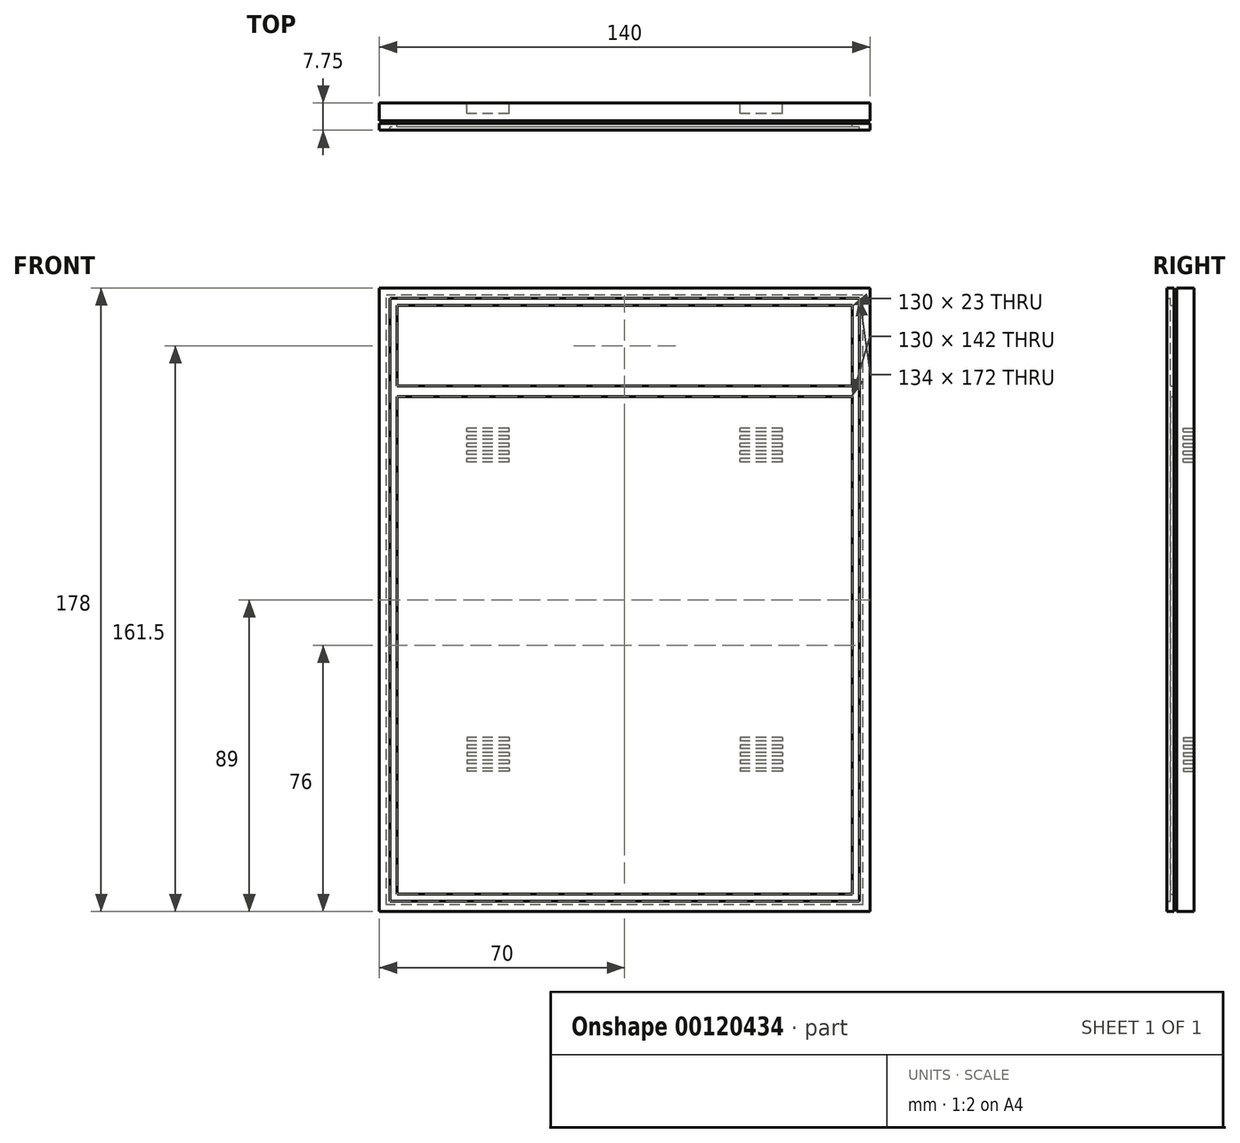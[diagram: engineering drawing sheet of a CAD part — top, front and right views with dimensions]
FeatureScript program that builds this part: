
annotation { "Feature Type Name" : "Feature", "Feature Type Description" : "" }
export const myFeature = defineFeature(function(context is Context, id is Id, definition is map)
    precondition{}
    {
        {
            var Q0;
            Q0=qCreatedBy(makeId("Front.planeOp"),FACE);
            var sketch = newSketch(context, id + "F0", { "sketchPlane" : qUnion([Q0])});
            skLineSegment(sketch, "E0.bottom", {"start": v(70, -89) * mm, "end": v(-70, -89) * mm});
            skLineSegment(sketch, "E0.top", {"start": v(70, 89) * mm, "end": v(-70, 89) * mm});
            skLineSegment(sketch, "E0.left", {"start": v(70, -89) * mm, "end": v(70, 89) * mm});
            skLineSegment(sketch, "E0.right", {"start": v(-70, -89) * mm, "end": v(-70, 89) * mm});
            skPoint(sketch, "E0.middle", {"position": v(0, 0) * mm});
            skLineSegment(sketch, "E1.0", {"start": v(67, 86) * mm, "end": v(-67, 86) * mm});
            skLineSegment(sketch, "E1.1", {"start": v(67, -86) * mm, "end": v(67, 86) * mm});
            skLineSegment(sketch, "E1.2", {"start": v(67, -86) * mm, "end": v(-67, -86) * mm});
            skLineSegment(sketch, "E1.3", {"start": v(-67, -86) * mm, "end": v(-67, 86) * mm});
            skLineSegment(sketch, "E2.bottom", {"start": v(65, -84) * mm, "end": v(-65, -84) * mm});
            skLineSegment(sketch, "E2.top", {"start": v(65, 61) * mm, "end": v(-65, 61) * mm});
            skLineSegment(sketch, "E2.right", {"start": v(-65, -84) * mm, "end": v(-65, 58) * mm});
            skPoint(sketch, "E2.middle", {"position": v(0, -11.5) * mm});
            skLineSegment(sketch, "E3.top", {"start": v(-65, 84) * mm, "end": v(65, 84) * mm});
            skLineSegment(sketch, "E3.left", {"start": v(-65, 61) * mm, "end": v(-65, 84) * mm});
            skLineSegment(sketch, "E3.right", {"start": v(65, 61) * mm, "end": v(65, 84) * mm});
            skLineSegment(sketch, "E4", {"start": v(-65, 58) * mm, "end": v(65, 58) * mm});
            skLineSegment(sketch, "E5", {"start": v(65, 58) * mm, "end": v(65, -84) * mm});
            skLineSegment(sketch, "E6.0", {"start": v(68, 87) * mm, "end": v(-68, 87) * mm});
            skLineSegment(sketch, "E6.1", {"start": v(68, -87) * mm, "end": v(68, 87) * mm});
            skLineSegment(sketch, "E6.2", {"start": v(68, -87) * mm, "end": v(-68, -87) * mm});
            skLineSegment(sketch, "E6.3", {"start": v(-68, -87) * mm, "end": v(-68, 87) * mm});
            skSolve(sketch);
        }
        {
            var Q0;
            Q0=makeQuery(id+"F0.imprint","IMPRINT",FACE,{"disambiguationData":[TD([[makeQuery(id+"F0.imprint","IMPRINT",EDGE,{"derivedFrom":sQuery(id+"F0.wireOp",EDGE,"E0.bottom")}),-1.0]])]});
            var Q1;
            Q1=makeQuery(id+"F0.imprint","IMPRINT",FACE,{"disambiguationData":[TD([[makeQuery(id+"F0.imprint","IMPRINT",EDGE,{"derivedFrom":sQuery(id+"F0.wireOp",EDGE,"E1.0")}),-1.0]])]});
            extrude(context, id + "F1", {"entities" : qUnion([Q0, Q1]), "depth" : 2 * mm});
        }
        {
            var Q0;
            Q0=makeQuery(id+"F0.imprint","IMPRINT",FACE,{"disambiguationData":[TD([[makeQuery(id+"F0.imprint","IMPRINT",EDGE,{"derivedFrom":sQuery(id+"F0.wireOp",EDGE,"E1.0")}),1.0]])]});
            extrude(context, id + "F2", {"entities" : qUnion([Q0]), "depth" : 1 * mm});
        }
        {
            var Q0;
            Q0=makeQuery(id+"F0.imprint","IMPRINT",FACE,{"disambiguationData":[TD([[makeQuery(id+"F0.imprint","IMPRINT",EDGE,{"derivedFrom":sQuery(id+"F0.wireOp",EDGE,"E2.bottom")}),-1.0]])]});
            extrude(context, id + "F3", {"entities" : qUnion([Q0]), "depth" : 1 * mm});
        }
        {
            var Q0;
            Q0=makeQuery(id+"F0.imprint","IMPRINT",FACE,{"disambiguationData":[TD([[makeQuery(id+"F0.imprint","IMPRINT",EDGE,{"derivedFrom":sQuery(id+"F0.wireOp",EDGE,"E2.top")}),-1.0]])]});
            extrude(context, id + "F4", {"entities" : qUnion([Q0]), "depth" : 1 * mm});
        }
        {
            var Q0;
            Q0=makeQuery(id+"F0.imprint","IMPRINT",FACE,{"disambiguationData":[TD([[makeQuery(id+"F0.imprint","IMPRINT",EDGE,{"derivedFrom":sQuery(id+"F0.wireOp",EDGE,"E1.0")}),-1.0]])]});
            extrude(context, id + "F5", {"entities" : qUnion([Q0]), "operationType" : NewBodyOperationType.ADD, "oppositeDirection" : true, "depth" : 0.75 * mm});
        }
        {
            var Q0;
            Q0=makeQuery(id+"F0.imprint","IMPRINT",FACE,{"disambiguationData":[TD([[makeQuery(id+"F0.imprint","IMPRINT",EDGE,{"derivedFrom":sQuery(id+"F0.wireOp",EDGE,"E0.bottom")}),-1.0]])]});
            var Q1;
            Q1=makeQuery(id+"F0.imprint","IMPRINT",FACE,{"disambiguationData":[TD([[makeQuery(id+"F0.imprint","IMPRINT",EDGE,{"derivedFrom":sQuery(id+"F0.wireOp",EDGE,"E1.0")}),-1.0]])]});
            var Q2;
            Q2=makeQuery(id+"F0.imprint","IMPRINT",FACE,{"disambiguationData":[TD([[makeQuery(id+"F0.imprint","IMPRINT",EDGE,{"derivedFrom":sQuery(id+"F0.wireOp",EDGE,"E1.0")}),1.0]])]});
            var Q3;
            Q3=makeQuery(id+"F0.imprint","IMPRINT",FACE,{"disambiguationData":[TD([[makeQuery(id+"F0.imprint","IMPRINT",EDGE,{"derivedFrom":sQuery(id+"F0.wireOp",EDGE,"E2.top")}),-1.0]])]});
            var Q4;
            Q4=makeQuery(id+"F0.imprint","IMPRINT",FACE,{"disambiguationData":[TD([[makeQuery(id+"F0.imprint","IMPRINT",EDGE,{"derivedFrom":sQuery(id+"F0.wireOp",EDGE,"E2.bottom")}),-1.0]])]});
            extrude(context, id + "F6", {"entities" : qUnion([Q0, Q1, Q2, Q3, Q4]), "oppositeDirection" : true, "depth" : 5 * mm});
        }
        {
            var Q0;
            Q0=makeQuery(id+"F6.opExtrude","SWEPT_BODY",BODY,{"disambiguationData":[OSD([sQuery(id+"F0.wireOp",EDGE,"E0.bottom"),sQuery(id+"F0.wireOp",EDGE,"E0.top"),sQuery(id+"F0.wireOp",EDGE,"E0.left"),sQuery(id+"F0.wireOp",EDGE,"E0.right")])]});
            transform(context, id + "F7", {"entities" : qUnion([Q0]), "transformType" : TransformType.TRANSLATION_3D, "dx" : 0 * mm, "dy" : 0.75 * mm, "dz" : 0 * mm, "makeCopy" : false});
        }
        {
            var Q0;
            Q0=makeQuery(id+"F6.opExtrude","CAP_FACE",FACE,{"disambiguationData":[OSD([sQuery(id+"F0.wireOp",EDGE,"E0.bottom"),sQuery(id+"F0.wireOp",EDGE,"E0.top"),sQuery(id+"F0.wireOp",EDGE,"E0.left"),sQuery(id+"F0.wireOp",EDGE,"E0.right")])],"isStart":false});
            var sketch = newSketch(context, id + "F8", { "sketchPlane" : qUnion([Q0])});
            skLineSegment(sketch, "E7.bottom", {"start": v(-45, -48) * mm, "end": v(-33, -48) * mm});
            skLineSegment(sketch, "E7.top", {"start": v(-45, -49) * mm, "end": v(-33, -49) * mm});
            skLineSegment(sketch, "E7.left", {"start": v(-45, -48) * mm, "end": v(-45, -49) * mm});
            skLineSegment(sketch, "E7.right", {"start": v(-33, -48) * mm, "end": v(-33, -49) * mm});
            skLineSegment(sketch, "E8.0.1.0", {"start": v(-45, -45.82) * mm, "end": v(-33, -45.82) * mm});
            skLineSegment(sketch, "E8.0.1.1", {"start": v(-45, -46.82) * mm, "end": v(-33, -46.82) * mm});
            skLineSegment(sketch, "E8.0.1.2", {"start": v(-33, -45.82) * mm, "end": v(-33, -46.82) * mm});
            skLineSegment(sketch, "E8.0.1.3", {"start": v(-45, -45.82) * mm, "end": v(-45, -46.82) * mm});
            skLineSegment(sketch, "E8.0.2.0", {"start": v(-45, -43.64) * mm, "end": v(-33, -43.64) * mm});
            skLineSegment(sketch, "E8.0.2.1", {"start": v(-45, -44.64) * mm, "end": v(-33, -44.64) * mm});
            skLineSegment(sketch, "E8.0.2.2", {"start": v(-33, -43.64) * mm, "end": v(-33, -44.64) * mm});
            skLineSegment(sketch, "E8.0.2.3", {"start": v(-45, -43.64) * mm, "end": v(-45, -44.64) * mm});
            skLineSegment(sketch, "E8.0.3.0", {"start": v(-45, -41.45) * mm, "end": v(-33, -41.45) * mm});
            skLineSegment(sketch, "E8.0.3.1", {"start": v(-45, -42.45) * mm, "end": v(-33, -42.45) * mm});
            skLineSegment(sketch, "E8.0.3.2", {"start": v(-33, -41.45) * mm, "end": v(-33, -42.45) * mm});
            skLineSegment(sketch, "E8.0.3.3", {"start": v(-45, -41.45) * mm, "end": v(-45, -42.45) * mm});
            skLineSegment(sketch, "E8.0.4.0", {"start": v(-45, -39.27) * mm, "end": v(-33, -39.27) * mm});
            skLineSegment(sketch, "E8.0.4.1", {"start": v(-45, -40.27) * mm, "end": v(-33, -40.27) * mm});
            skLineSegment(sketch, "E8.0.4.2", {"start": v(-33, -39.27) * mm, "end": v(-33, -40.27) * mm});
            skLineSegment(sketch, "E8.0.4.3", {"start": v(-45, -39.27) * mm, "end": v(-45, -40.27) * mm});
            skLineSegment(sketch, "E8.1.0.0", {"start": v(33, -48) * mm, "end": v(45, -48) * mm});
            skLineSegment(sketch, "E8.1.0.1", {"start": v(33, -49) * mm, "end": v(45, -49) * mm});
            skLineSegment(sketch, "E8.1.0.2", {"start": v(45, -48) * mm, "end": v(45, -49) * mm});
            skLineSegment(sketch, "E8.1.0.3", {"start": v(33, -48) * mm, "end": v(33, -49) * mm});
            skLineSegment(sketch, "E8.1.1.0", {"start": v(33, -45.82) * mm, "end": v(45, -45.82) * mm});
            skLineSegment(sketch, "E8.1.1.1", {"start": v(33, -46.82) * mm, "end": v(45, -46.82) * mm});
            skLineSegment(sketch, "E8.1.1.2", {"start": v(45, -45.82) * mm, "end": v(45, -46.82) * mm});
            skLineSegment(sketch, "E8.1.1.3", {"start": v(33, -45.82) * mm, "end": v(33, -46.82) * mm});
            skLineSegment(sketch, "E8.1.2.0", {"start": v(33, -43.64) * mm, "end": v(45, -43.64) * mm});
            skLineSegment(sketch, "E8.1.2.1", {"start": v(33, -44.64) * mm, "end": v(45, -44.64) * mm});
            skLineSegment(sketch, "E8.1.2.2", {"start": v(45, -43.64) * mm, "end": v(45, -44.64) * mm});
            skLineSegment(sketch, "E8.1.2.3", {"start": v(33, -43.64) * mm, "end": v(33, -44.64) * mm});
            skLineSegment(sketch, "E8.1.3.0", {"start": v(33, -41.45) * mm, "end": v(45, -41.45) * mm});
            skLineSegment(sketch, "E8.1.3.1", {"start": v(33, -42.45) * mm, "end": v(45, -42.45) * mm});
            skLineSegment(sketch, "E8.1.3.2", {"start": v(45, -41.45) * mm, "end": v(45, -42.45) * mm});
            skLineSegment(sketch, "E8.1.3.3", {"start": v(33, -41.45) * mm, "end": v(33, -42.45) * mm});
            skLineSegment(sketch, "E8.1.4.0", {"start": v(33, -39.27) * mm, "end": v(45, -39.27) * mm});
            skLineSegment(sketch, "E8.1.4.1", {"start": v(33, -40.27) * mm, "end": v(45, -40.27) * mm});
            skLineSegment(sketch, "E8.1.4.2", {"start": v(45, -39.27) * mm, "end": v(45, -40.27) * mm});
            skLineSegment(sketch, "E8.1.4.3", {"start": v(33, -39.27) * mm, "end": v(33, -40.27) * mm});
            skLineSegment(sketch, "E8.direction1", {"start": v(-45, -48) * mm, "end": v(33, -48) * mm, "construction": true});
            skLineSegment(sketch, "E8.direction2", {"start": v(-45, -48) * mm, "end": v(-45, -45.82) * mm, "construction": true});
            skLineSegment(sketch, "E9.MirrorCS", {"start": v(-45, 48) * mm, "end": v(-45, 45.82) * mm, "construction": true});
            skLineSegment(sketch, "E10.MirrorCS", {"start": v(-33, 41.45) * mm, "end": v(-33, 42.45) * mm});
            skLineSegment(sketch, "E11.MirrorCS", {"start": v(-45, 41.45) * mm, "end": v(-45, 42.45) * mm});
            skLineSegment(sketch, "E12.MirrorCS", {"start": v(-45, 48) * mm, "end": v(-45, 49) * mm});
            skLineSegment(sketch, "E13.MirrorCS", {"start": v(-45, 45.82) * mm, "end": v(-45, 46.82) * mm});
            skLineSegment(sketch, "E14.MirrorCS", {"start": v(-33, 48) * mm, "end": v(-33, 49) * mm});
            skLineSegment(sketch, "E15.MirrorCS", {"start": v(-45, 39.27) * mm, "end": v(-45, 40.27) * mm});
            skLineSegment(sketch, "E16.MirrorCS", {"start": v(-45, 43.64) * mm, "end": v(-45, 44.64) * mm});
            skLineSegment(sketch, "E17.MirrorCS", {"start": v(-33, 43.64) * mm, "end": v(-33, 44.64) * mm});
            skLineSegment(sketch, "E18.MirrorCS", {"start": v(-33, 45.82) * mm, "end": v(-33, 46.82) * mm});
            skLineSegment(sketch, "E19.MirrorCS", {"start": v(-33, 39.27) * mm, "end": v(-33, 40.27) * mm});
            skLineSegment(sketch, "E20.MirrorCS", {"start": v(-45, 40.27) * mm, "end": v(-33, 40.27) * mm});
            skLineSegment(sketch, "E21.MirrorCS", {"start": v(-45, 42.45) * mm, "end": v(-33, 42.45) * mm});
            skLineSegment(sketch, "E22.MirrorCS", {"start": v(-45, 48) * mm, "end": v(-33, 48) * mm});
            skLineSegment(sketch, "E23.MirrorCS", {"start": v(-45, 49) * mm, "end": v(-33, 49) * mm});
            skLineSegment(sketch, "E24.MirrorCS", {"start": v(-45, 45.82) * mm, "end": v(-33, 45.82) * mm});
            skLineSegment(sketch, "E25.MirrorCS", {"start": v(-45, 41.45) * mm, "end": v(-33, 41.45) * mm});
            skLineSegment(sketch, "E26.MirrorCS", {"start": v(-45, 44.64) * mm, "end": v(-33, 44.64) * mm});
            skLineSegment(sketch, "E27.MirrorCS", {"start": v(-45, 43.64) * mm, "end": v(-33, 43.64) * mm});
            skLineSegment(sketch, "E28.MirrorCS", {"start": v(-45, 39.27) * mm, "end": v(-33, 39.27) * mm});
            skLineSegment(sketch, "E29.MirrorCS", {"start": v(-45, 46.82) * mm, "end": v(-33, 46.82) * mm});
            skLineSegment(sketch, "E30.MirrorCS", {"start": v(33, 48) * mm, "end": v(33, 49) * mm});
            skLineSegment(sketch, "E31.MirrorCS", {"start": v(33, 43.64) * mm, "end": v(33, 44.64) * mm});
            skLineSegment(sketch, "E32.MirrorCS", {"start": v(45, 41.45) * mm, "end": v(45, 42.45) * mm});
            skLineSegment(sketch, "E33.MirrorCS", {"start": v(33, 45.82) * mm, "end": v(33, 46.82) * mm});
            skLineSegment(sketch, "E34.MirrorCS", {"start": v(45, 48) * mm, "end": v(45, 49) * mm});
            skLineSegment(sketch, "E35.MirrorCS", {"start": v(45, 39.27) * mm, "end": v(45, 40.27) * mm});
            skLineSegment(sketch, "E36.MirrorCS", {"start": v(45, 45.82) * mm, "end": v(45, 46.82) * mm});
            skLineSegment(sketch, "E37.MirrorCS", {"start": v(45, 43.64) * mm, "end": v(45, 44.64) * mm});
            skLineSegment(sketch, "E38.MirrorCS", {"start": v(33, 41.45) * mm, "end": v(33, 42.45) * mm});
            skLineSegment(sketch, "E39.MirrorCS", {"start": v(33, 39.27) * mm, "end": v(33, 40.27) * mm});
            skLineSegment(sketch, "E40.MirrorCS", {"start": v(33, 48) * mm, "end": v(45, 48) * mm});
            skLineSegment(sketch, "E41.MirrorCS", {"start": v(33, 44.64) * mm, "end": v(45, 44.64) * mm});
            skLineSegment(sketch, "E42.MirrorCS", {"start": v(33, 39.27) * mm, "end": v(45, 39.27) * mm});
            skLineSegment(sketch, "E43.MirrorCS", {"start": v(33, 46.82) * mm, "end": v(45, 46.82) * mm});
            skLineSegment(sketch, "E44.MirrorCS", {"start": v(33, 45.82) * mm, "end": v(45, 45.82) * mm});
            skLineSegment(sketch, "E45.MirrorCS", {"start": v(33, 41.45) * mm, "end": v(45, 41.45) * mm});
            skLineSegment(sketch, "E46.MirrorCS", {"start": v(33, 49) * mm, "end": v(45, 49) * mm});
            skLineSegment(sketch, "E47.MirrorCS", {"start": v(33, 40.27) * mm, "end": v(45, 40.27) * mm});
            skLineSegment(sketch, "E48.MirrorCS", {"start": v(33, 43.64) * mm, "end": v(45, 43.64) * mm});
            skLineSegment(sketch, "E49.MirrorCS", {"start": v(33, 42.45) * mm, "end": v(45, 42.45) * mm});
            skSolve(sketch);
        }
        {
            var Q0;
            Q0=qSketchRegion(id+"F8",true);
            extrude(context, id + "F9", {"entities" : qUnion([Q0]), "operationType" : NewBodyOperationType.REMOVE, "oppositeDirection" : true, "depth" : 3 * mm});
        }
    });
